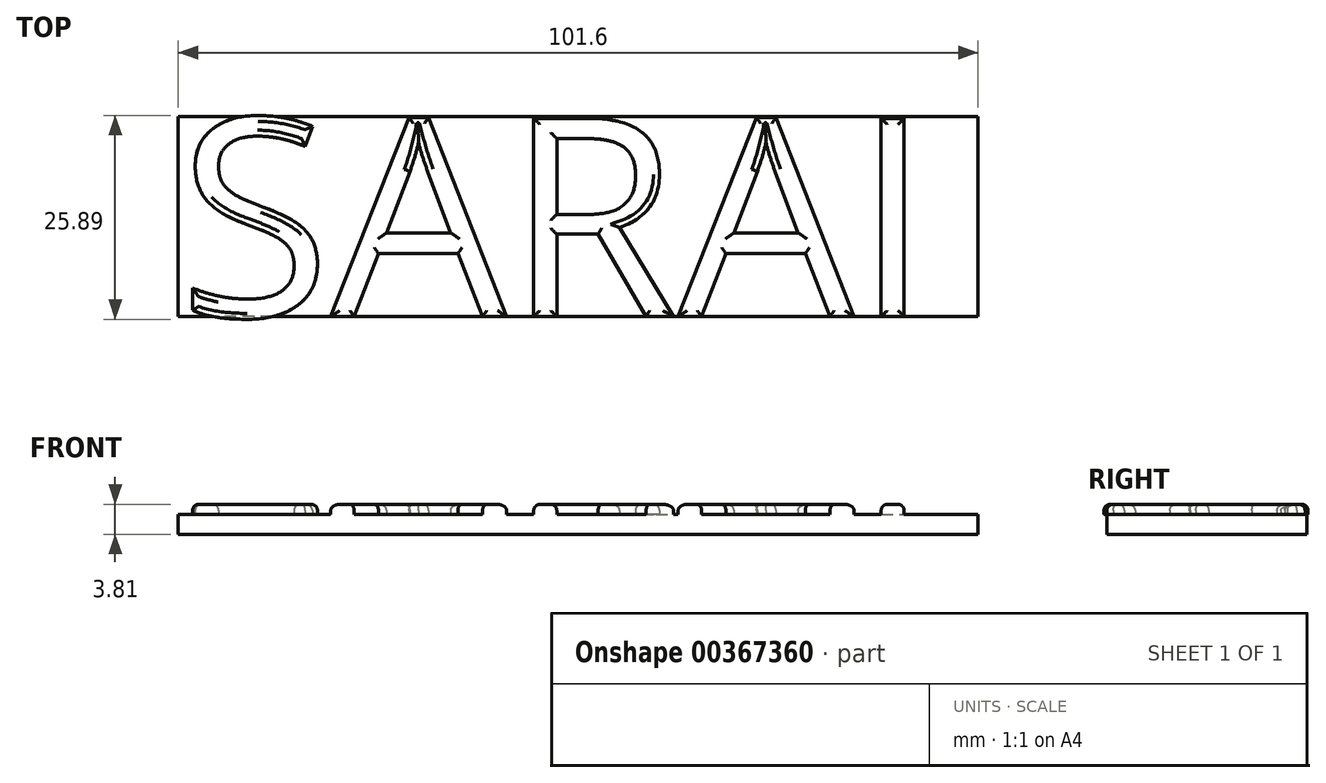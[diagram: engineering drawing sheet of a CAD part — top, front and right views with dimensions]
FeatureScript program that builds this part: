
annotation { "Feature Type Name" : "Feature", "Feature Type Description" : "" }
export const myFeature = defineFeature(function(context is Context, id is Id, definition is map)
    precondition{}
    {
        {
            var Q0;
            Q0=qCreatedBy(makeId("Top.planeOp"),FACE);
            var sketch = newSketch(context, id + "F0", { "sketchPlane" : qUnion([Q0])});
            skLineSegment(sketch, "E0.bottom", {"start": v(50.8, 12.7) * mm, "end": v(-50.8, 12.7) * mm});
            skLineSegment(sketch, "E0.top", {"start": v(50.8, -12.7) * mm, "end": v(-50.8, -12.7) * mm});
            skLineSegment(sketch, "E0.left", {"start": v(50.8, 12.7) * mm, "end": v(50.8, -12.7) * mm});
            skLineSegment(sketch, "E0.right", {"start": v(-50.8, 12.7) * mm, "end": v(-50.8, -12.7) * mm});
            skPoint(sketch, "E0.middle", {"position": v(0, 0) * mm});
            skSolve(sketch);
        }
        {
            var Q0;
            Q0 = qSketchRegion(id + "F0", true);
            extrude(context, id + "F1", {"entities" : qUnion([Q0]), "depth" : 2.54 * mm});
        }
        {
            var Q0;
            Q0=makeQuery(id+"F1.opExtrude","CAP_FACE",FACE,{"disambiguationData":[OSD([sQuery(id+"F0.wireOp",EDGE,"E0.bottom"),sQuery(id+"F0.wireOp",EDGE,"E0.top"),sQuery(id+"F0.wireOp",EDGE,"E0.left"),sQuery(id+"F0.wireOp",EDGE,"E0.right")])],"isStart":false});
            var sketch = newSketch(context, id + "F2", { "sketchPlane" : qUnion([Q0])});
            skText(sketch, "E1", { "text": "SARAI", "fontName": "OpenSans-Regular.ttf"});
            const initialGuessF2  = {"E1": [-0.0508, -0.0127, 1, 0, 0.0254]};
            skSetInitialGuess(sketch, initialGuessF2);
            skSolve(sketch);
        }
        {
            var Q0;
            Q0 = qSketchRegion(id + "F2", true);
            extrude(context, id + "F3", {"entities" : qUnion([Q0]), "operationType" : NewBodyOperationType.ADD, "depth" : 1.27 * mm});
        }
        {
            var Q0;
            Q0=makeQuery(id+"F3.opExtrude","CAP_FACE",FACE,{"disambiguationData":[OSD([sQuery(id+"F2.wireOp",EDGE,"E1.sketch_text.stroke-69"),sQuery(id+"F2.wireOp",EDGE,"E1.sketch_text.stroke-70"),sQuery(id+"F2.wireOp",EDGE,"E1.sketch_text.stroke-71"),sQuery(id+"F2.wireOp",EDGE,"E1.sketch_text.stroke-72")])],"isStart":false});
            var Q1;
            Q1=makeQuery(id+"F3.opExtrude","CAP_FACE",FACE,{"disambiguationData":[OSD([sQuery(id+"F2.wireOp",EDGE,"E1.sketch_text.stroke-56"),sQuery(id+"F2.wireOp",EDGE,"E1.sketch_text.stroke-57"),sQuery(id+"F2.wireOp",EDGE,"E1.sketch_text.stroke-58"),sQuery(id+"F2.wireOp",EDGE,"E1.sketch_text.stroke-59"),sQuery(id+"F2.wireOp",EDGE,"E1.sketch_text.stroke-60"),sQuery(id+"F2.wireOp",EDGE,"E1.sketch_text.stroke-61"),sQuery(id+"F2.wireOp",EDGE,"E1.sketch_text.stroke-62"),sQuery(id+"F2.wireOp",EDGE,"E1.sketch_text.stroke-63"),sQuery(id+"F2.wireOp",EDGE,"E1.sketch_text.stroke-64"),sQuery(id+"F2.wireOp",EDGE,"E1.sketch_text.stroke-65"),sQuery(id+"F2.wireOp",EDGE,"E1.sketch_text.stroke-66"),sQuery(id+"F2.wireOp",EDGE,"E1.sketch_text.stroke-67"),sQuery(id+"F2.wireOp",EDGE,"E1.sketch_text.stroke-68")])],"isStart":false});
            var Q2;
            Q2=makeQuery(id+"F3.opExtrude","CAP_FACE",FACE,{"disambiguationData":[OSD([sQuery(id+"F2.wireOp",EDGE,"E1.sketch_text.stroke-38"),sQuery(id+"F2.wireOp",EDGE,"E1.sketch_text.stroke-39"),sQuery(id+"F2.wireOp",EDGE,"E1.sketch_text.stroke-40"),sQuery(id+"F2.wireOp",EDGE,"E1.sketch_text.stroke-41"),sQuery(id+"F2.wireOp",EDGE,"E1.sketch_text.stroke-42"),sQuery(id+"F2.wireOp",EDGE,"E1.sketch_text.stroke-43"),sQuery(id+"F2.wireOp",EDGE,"E1.sketch_text.stroke-44"),sQuery(id+"F2.wireOp",EDGE,"E1.sketch_text.stroke-45"),sQuery(id+"F2.wireOp",EDGE,"E1.sketch_text.stroke-46"),sQuery(id+"F2.wireOp",EDGE,"E1.sketch_text.stroke-47"),sQuery(id+"F2.wireOp",EDGE,"E1.sketch_text.stroke-48"),sQuery(id+"F2.wireOp",EDGE,"E1.sketch_text.stroke-49"),sQuery(id+"F2.wireOp",EDGE,"E1.sketch_text.stroke-50"),sQuery(id+"F2.wireOp",EDGE,"E1.sketch_text.stroke-51"),sQuery(id+"F2.wireOp",EDGE,"E1.sketch_text.stroke-52"),sQuery(id+"F2.wireOp",EDGE,"E1.sketch_text.stroke-53"),sQuery(id+"F2.wireOp",EDGE,"E1.sketch_text.stroke-54"),sQuery(id+"F2.wireOp",EDGE,"E1.sketch_text.stroke-55")])],"isStart":false});
            var Q3;
            Q3=makeQuery(id+"F3.opExtrude","CAP_FACE",FACE,{"disambiguationData":[OSD([sQuery(id+"F2.wireOp",EDGE,"E1.sketch_text.stroke-25"),sQuery(id+"F2.wireOp",EDGE,"E1.sketch_text.stroke-26"),sQuery(id+"F2.wireOp",EDGE,"E1.sketch_text.stroke-27"),sQuery(id+"F2.wireOp",EDGE,"E1.sketch_text.stroke-28"),sQuery(id+"F2.wireOp",EDGE,"E1.sketch_text.stroke-29"),sQuery(id+"F2.wireOp",EDGE,"E1.sketch_text.stroke-30"),sQuery(id+"F2.wireOp",EDGE,"E1.sketch_text.stroke-31"),sQuery(id+"F2.wireOp",EDGE,"E1.sketch_text.stroke-32"),sQuery(id+"F2.wireOp",EDGE,"E1.sketch_text.stroke-33"),sQuery(id+"F2.wireOp",EDGE,"E1.sketch_text.stroke-34"),sQuery(id+"F2.wireOp",EDGE,"E1.sketch_text.stroke-35"),sQuery(id+"F2.wireOp",EDGE,"E1.sketch_text.stroke-36"),sQuery(id+"F2.wireOp",EDGE,"E1.sketch_text.stroke-37")])],"isStart":false});
            var Q4;
            Q4=makeQuery(id+"F3.opExtrude","CAP_FACE",FACE,{"disambiguationData":[OSD([sQuery(id+"F2.wireOp",EDGE,"E1.sketch_text.stroke-0"),sQuery(id+"F2.wireOp",EDGE,"E1.sketch_text.stroke-1"),sQuery(id+"F2.wireOp",EDGE,"E1.sketch_text.stroke-2"),sQuery(id+"F2.wireOp",EDGE,"E1.sketch_text.stroke-3"),sQuery(id+"F2.wireOp",EDGE,"E1.sketch_text.stroke-4"),sQuery(id+"F2.wireOp",EDGE,"E1.sketch_text.stroke-5"),sQuery(id+"F2.wireOp",EDGE,"E1.sketch_text.stroke-6"),sQuery(id+"F2.wireOp",EDGE,"E1.sketch_text.stroke-7"),sQuery(id+"F2.wireOp",EDGE,"E1.sketch_text.stroke-8"),sQuery(id+"F2.wireOp",EDGE,"E1.sketch_text.stroke-9"),sQuery(id+"F2.wireOp",EDGE,"E1.sketch_text.stroke-10"),sQuery(id+"F2.wireOp",EDGE,"E1.sketch_text.stroke-11"),sQuery(id+"F2.wireOp",EDGE,"E1.sketch_text.stroke-12"),sQuery(id+"F2.wireOp",EDGE,"E1.sketch_text.stroke-13"),sQuery(id+"F2.wireOp",EDGE,"E1.sketch_text.stroke-14"),sQuery(id+"F2.wireOp",EDGE,"E1.sketch_text.stroke-15"),sQuery(id+"F2.wireOp",EDGE,"E1.sketch_text.stroke-16"),sQuery(id+"F2.wireOp",EDGE,"E1.sketch_text.stroke-17"),sQuery(id+"F2.wireOp",EDGE,"E1.sketch_text.stroke-18"),sQuery(id+"F2.wireOp",EDGE,"E1.sketch_text.stroke-19"),sQuery(id+"F2.wireOp",EDGE,"E1.sketch_text.stroke-20"),sQuery(id+"F2.wireOp",EDGE,"E1.sketch_text.stroke-21"),sQuery(id+"F2.wireOp",EDGE,"E1.sketch_text.stroke-22"),sQuery(id+"F2.wireOp",EDGE,"E1.sketch_text.stroke-23"),sQuery(id+"F2.wireOp",EDGE,"E1.sketch_text.stroke-24")])],"isStart":false});
            fillet(context, id + "F4", {"entities" : qUnion([Q0, Q1, Q2, Q3, Q4]), "radius" : 0.76 * mm, "tangentPropagation" : true, "allowEdgeOverflow" : false});
        }
    });
